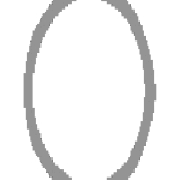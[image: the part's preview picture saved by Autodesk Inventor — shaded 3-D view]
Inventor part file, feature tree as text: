
AUTODESK INVENTOR PART (.ipt)
format: ipt  version: 2021 (Build 250183000, 183)  size: 152,576 bytes
history: native  units: in
note: dims shown in document units (in); Inventor stores cm internally (conversion verified against a paired STEP export)
features: other x5, sketch x2, sweep x1, plane x1
ambient origin geometry x8: Origin, YZ Plane, XZ Plane, XY Plane, X Axis, Y Axis, Z Axis, Center Point
bodies: Solid1 (feature_tree), Body (feature_tree)
feature tree (9):
  other  "Driven Length"
  other  "Frame Generator"
  other  "Start Plane"
  other  "End Plane"
  sweep  "Sweep Path"
  other  "Orientation Work Plane"
  sketch  "Sketch2"  dims[d0=1.0in d1=0.065in]
  plane  "Work Plane3"
  sketch  "Sketch3"  dims[d2=16.4521in d4=-0.0in d5=16.4521in d8=90.0deg d9=16.4521in d10=0.0in d11=0.0in]
